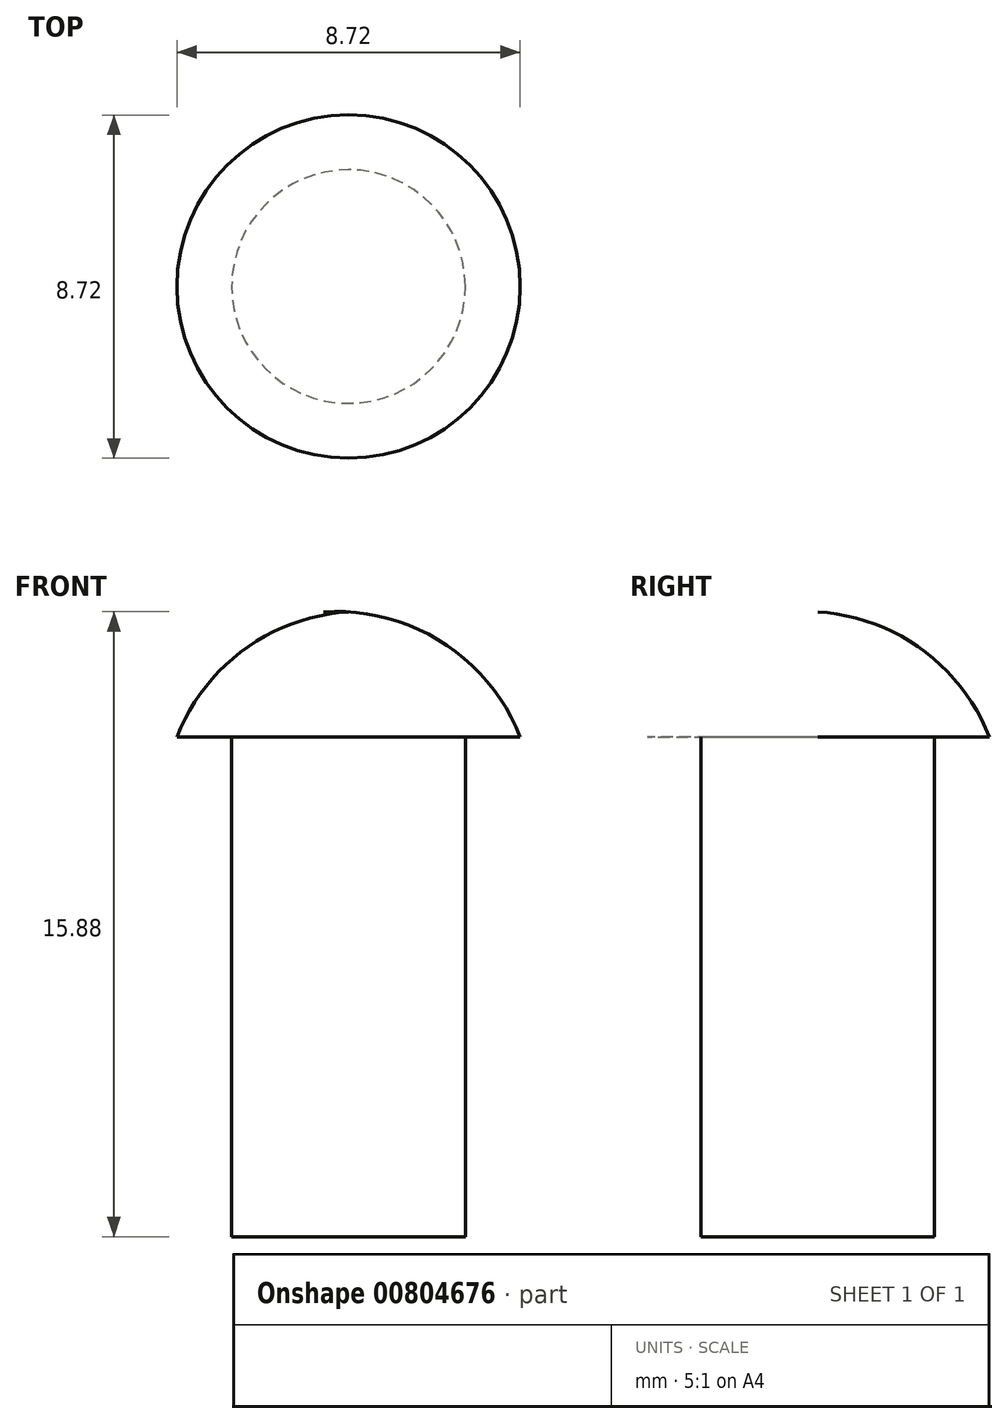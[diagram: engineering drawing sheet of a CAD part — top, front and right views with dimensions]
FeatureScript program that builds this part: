
annotation { "Feature Type Name" : "Feature", "Feature Type Description" : "" }
export const myFeature = defineFeature(function(context is Context, id is Id, definition is map)
    precondition{}
    {
        {
            var Q0;
            Q0=qCreatedBy(makeId("Front.planeOp"),FACE);
            var sketch = newSketch(context, id + "F0", { "sketchPlane" : qUnion([Q0])});
            skLineSegment(sketch, "E0.bottom", {"start": v(0, 0) * mm, "end": v(2.97, 0) * mm});
            skLineSegment(sketch, "E0.left", {"start": v(0, 0) * mm, "end": v(0, 12.7) * mm});
            skLineSegment(sketch, "E0.right", {"start": v(2.97, 0) * mm, "end": v(2.97, 12.7) * mm});
            skLineSegment(sketch, "E1", {"start": v(0, 12.7) * mm, "end": v(0, 15.88) * mm});
            skLineSegment(sketch, "E2", {"start": v(2.97, 12.7) * mm, "end": v(4.36, 12.7) * mm});
            skArc(sketch, "E3", {"start": v(4.36, 12.7) * mm, "mid": v(2.64, 14.92) * mm, "end": v(0, 15.88) * mm});
            skLineSegment(sketch, "E4", {"start": v(0, -10.8) * mm, "end": v(0, 23.6) * mm, "construction": true});
            skSolve(sketch);
        }
        {
            var Q0;
            Q0=makeQuery(id+"F0.imprint","IMPRINT",FACE,{"disambiguationData":[TD([[makeQuery(id+"F0.imprint","IMPRINT",EDGE,{"derivedFrom":sQuery(id+"F0.wireOp",EDGE,"E0.bottom")}),1.0]])]});
            var Q1;
            Q1=sQuery(id+"F0.wireOp",EDGE,"E4");
            revolve(context, id + "F1", {"surfaceOperationType" : NewSurfaceOperationType.NEW, "entities" : qUnion([Q0]), "axis" : qUnion([Q1]), "revolveType" : RevolveType.FULL});
        }
    });
